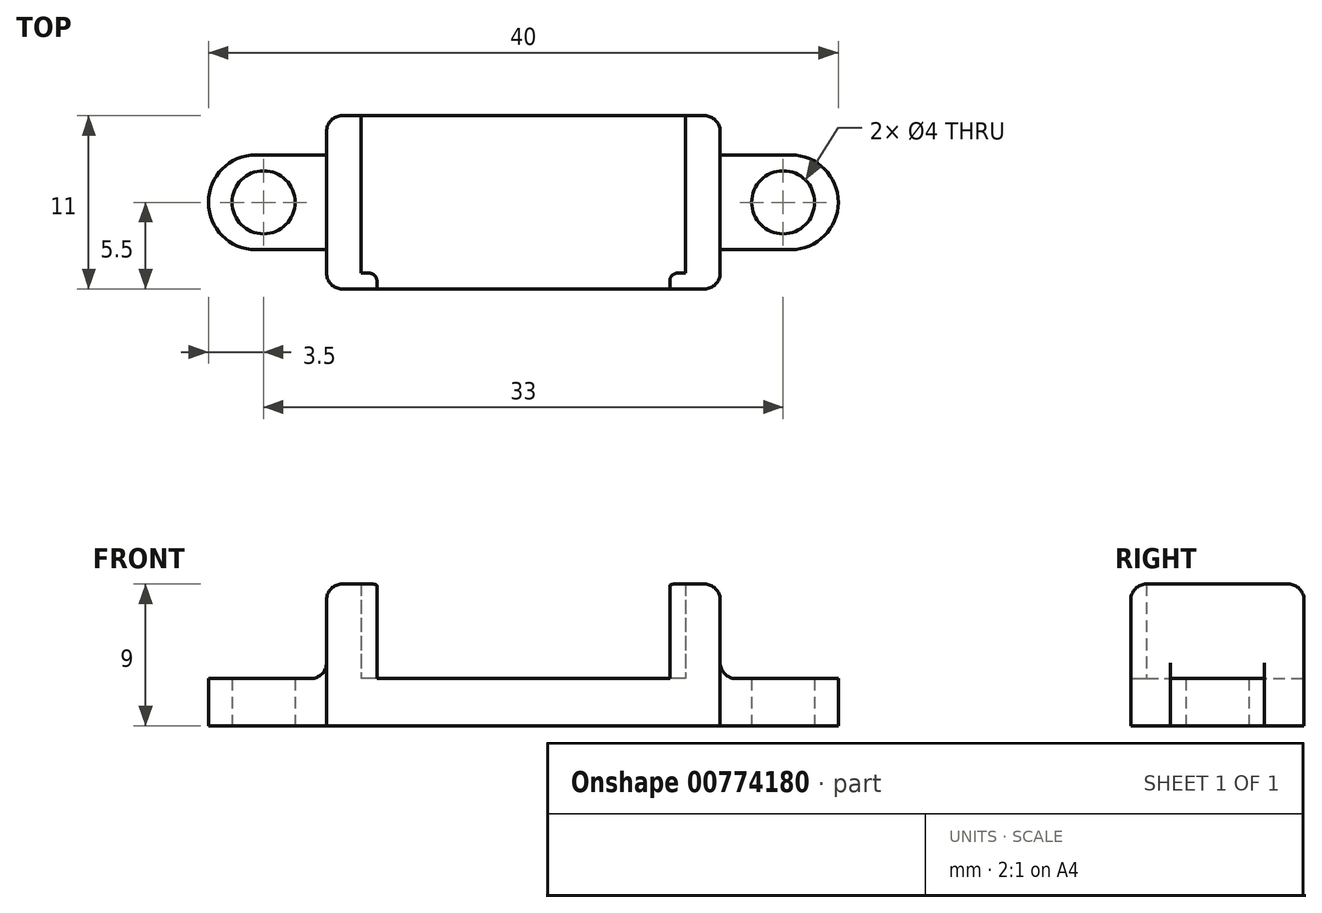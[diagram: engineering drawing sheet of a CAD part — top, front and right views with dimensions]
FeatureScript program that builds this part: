
annotation { "Feature Type Name" : "Feature", "Feature Type Description" : "" }
export const myFeature = defineFeature(function(context is Context, id is Id, definition is map)
    precondition{}
    {
        {
            var Q0;
            Q0=qCreatedBy(makeId("Top.planeOp"),FACE);
            var sketch = newSketch(context, id + "F0", { "sketchPlane" : qUnion([Q0])});
            skLineSegment(sketch, "E0.bottom", {"start": v(12.5, -5.5) * mm, "end": v(-12.5, -5.5) * mm});
            skLineSegment(sketch, "E0.top", {"start": v(12.5, 5.5) * mm, "end": v(-12.5, 5.5) * mm});
            skLineSegment(sketch, "E0.left", {"start": v(12.5, -5.5) * mm, "end": v(12.5, 5.5) * mm});
            skLineSegment(sketch, "E0.right", {"start": v(-12.5, -5.5) * mm, "end": v(-12.5, 5.5) * mm});
            skPoint(sketch, "E0.middle", {"position": v(0, 0) * mm});
            skSolve(sketch);
        }
        {
            var Q0;
            Q0 = qSketchRegion(id + "F0", true);
            extrude(context, id + "F1", {"entities" : qUnion([Q0]), "depth" : 9 * mm, "offsetDistance" : 25 * mm});
        }
        {
            var Q0;
            Q0=qCreatedBy(makeId("Top.planeOp"),FACE);
            var sketch = newSketch(context, id + "F2", { "sketchPlane" : qUnion([Q0])});
            skLineSegment(sketch, "E1.bottom", {"start": v(10.3, -5) * mm, "end": v(-10.3, -5) * mm});
            skLineSegment(sketch, "E1.top", {"start": v(10.3, 5) * mm, "end": v(-10.3, 5) * mm});
            skLineSegment(sketch, "E1.left", {"start": v(10.3, -5) * mm, "end": v(10.3, 5) * mm});
            skLineSegment(sketch, "E1.right", {"start": v(-10.3, -5) * mm, "end": v(-10.3, 5) * mm});
            skPoint(sketch, "E1.middle", {"position": v(0, 0) * mm});
            skSolve(sketch);
        }
        {
            var Q0;
            Q0 = qSketchRegion(id + "F2", true);
            extrude(context, id + "F3", {"entities" : qUnion([Q0]), "depth" : 6 * mm, "offsetDistance" : 25 * mm});
        }
        {
            var Q0;
            Q0=qCreatedBy(makeId("Top.planeOp"),FACE);
            var sketch = newSketch(context, id + "F4", { "sketchPlane" : qUnion([Q0])});
            skLineSegment(sketch, "E2.bottom", {"start": v(9.3, -5) * mm, "end": v(-9.3, -5) * mm});
            skLineSegment(sketch, "E2.top", {"start": v(9.3, 5) * mm, "end": v(-9.3, 5) * mm});
            skLineSegment(sketch, "E2.left", {"start": v(9.3, -5) * mm, "end": v(9.3, 5) * mm});
            skLineSegment(sketch, "E2.right", {"start": v(-9.3, -5) * mm, "end": v(-9.3, 5) * mm});
            skPoint(sketch, "E2.middle", {"position": v(0, 0) * mm});
            skSolve(sketch);
        }
        {
            var Q0;
            Q0 = qSketchRegion(id + "F4", true);
            extrude(context, id + "F5", {"entities" : qUnion([Q0]), "depth" : 6 * mm, "offsetDistance" : 25 * mm});
        }
        {
            var Q0;
            Q0=makeQuery(id+"F5.opExtrude","SWEPT_BODY",BODY,{"disambiguationData":[OSD([sQuery(id+"F4.wireOp",EDGE,"E2.bottom"),sQuery(id+"F4.wireOp",EDGE,"E2.top"),sQuery(id+"F4.wireOp",EDGE,"E2.left"),sQuery(id+"F4.wireOp",EDGE,"E2.right")])]});
            transform(context, id + "F6", {"entities" : qUnion([Q0]), "transformType" : TransformType.TRANSLATION_3D, "dx" : 0 * mm, "dy" : -5 * mm, "dz" : 0 * mm, "makeCopy" : false});
        }
        {
            var Q0;
            Q0=makeQuery(id+"F3.opExtrude","SWEPT_BODY",BODY,{"disambiguationData":[OSD([sQuery(id+"F2.wireOp",EDGE,"E1.bottom"),sQuery(id+"F2.wireOp",EDGE,"E1.top"),sQuery(id+"F2.wireOp",EDGE,"E1.left"),sQuery(id+"F2.wireOp",EDGE,"E1.right")])]});
            var Q1;
            Q1=makeQuery(id+"F5.opExtrude","SWEPT_BODY",BODY,{"disambiguationData":[OSD([sQuery(id+"F4.wireOp",EDGE,"E2.bottom"),sQuery(id+"F4.wireOp",EDGE,"E2.top"),sQuery(id+"F4.wireOp",EDGE,"E2.left"),sQuery(id+"F4.wireOp",EDGE,"E2.right")])]});
            booleanBodies(context, id + "F7", {"operationType" : BooleanOperationType.UNION, "tools" : qUnion([Q0, Q1])});
        }
        {
            var Q0;
            Q0=makeQuery(id+"F7.opBoolean","INTERSECT",EDGE,{"derivedFrom":[makeQuery(id+"F3.opExtrude","SWEPT_FACE",FACE,{"disambiguationData":[OSD([sQuery(id+"F2.wireOp",EDGE,"E1.bottom")])]}),makeQuery(id+"F5.opExtrude","SWEPT_FACE",FACE,{"disambiguationData":[OSD([sQuery(id+"F4.wireOp",EDGE,"E2.right")])]})]});
            var Q1;
            Q1=makeQuery(id+"F7.opBoolean","INTERSECT",EDGE,{"derivedFrom":[makeQuery(id+"F3.opExtrude","SWEPT_FACE",FACE,{"disambiguationData":[OSD([sQuery(id+"F2.wireOp",EDGE,"E1.bottom")])]}),makeQuery(id+"F5.opExtrude","SWEPT_FACE",FACE,{"disambiguationData":[OSD([sQuery(id+"F4.wireOp",EDGE,"E2.left")])]})]});
            fillet(context, id + "F8", {"entities" : qUnion([Q0, Q1]), "radius" : 0.5 * mm, "tangentPropagation" : true, "allowEdgeOverflow" : false});
        }
        {
            var Q0;
            Q0=makeQuery(id+"F3.opExtrude","SWEPT_BODY",BODY,{"disambiguationData":[OSD([sQuery(id+"F2.wireOp",EDGE,"E1.bottom"),sQuery(id+"F2.wireOp",EDGE,"E1.top"),sQuery(id+"F2.wireOp",EDGE,"E1.left"),sQuery(id+"F2.wireOp",EDGE,"E1.right")])]});
            transform(context, id + "F9", {"entities" : qUnion([Q0]), "transformType" : TransformType.TRANSLATION_3D, "dx" : 0 * mm, "dy" : .5 * mm, "dz" : 3 * mm, "makeCopy" : false});
        }
        {
            var Q0;
            Q0=makeQuery(id+"F3.opExtrude","SWEPT_BODY",BODY,{"disambiguationData":[OSD([sQuery(id+"F2.wireOp",EDGE,"E1.bottom"),sQuery(id+"F2.wireOp",EDGE,"E1.top"),sQuery(id+"F2.wireOp",EDGE,"E1.left"),sQuery(id+"F2.wireOp",EDGE,"E1.right")])]});
            var Q1;
            Q1=makeQuery(id+"F1.opExtrude","SWEPT_BODY",BODY,{"disambiguationData":[OSD([sQuery(id+"F0.wireOp",EDGE,"E0.bottom"),sQuery(id+"F0.wireOp",EDGE,"E0.top"),sQuery(id+"F0.wireOp",EDGE,"E0.left"),sQuery(id+"F0.wireOp",EDGE,"E0.right")])]});
            booleanBodies(context, id + "F10", {"operationType" : BooleanOperationType.SUBTRACTION, "tools" : qUnion([Q0]), "targets" : qUnion([Q1])});
        }
        {
            var Q0;
            Q0=qCreatedBy(makeId("Top.planeOp"),FACE);
            var sketch = newSketch(context, id + "F11", { "sketchPlane" : qUnion([Q0])});
            skLineSegment(sketch, "E3.bottom", {"start": v(20, -3) * mm, "end": v(-20, -3) * mm});
            skLineSegment(sketch, "E3.top", {"start": v(20, 3) * mm, "end": v(-20, 3) * mm});
            skLineSegment(sketch, "E3.left", {"start": v(20, -3) * mm, "end": v(20, 3) * mm});
            skLineSegment(sketch, "E3.right", {"start": v(-20, -3) * mm, "end": v(-20, 3) * mm});
            skPoint(sketch, "E3.middle", {"position": v(0, 0) * mm});
            skLineSegment(sketch, "E4", {"start": v(0, 0) * mm, "end": v(-16.5, 0) * mm});
            skLineSegment(sketch, "E5", {"start": v(0, 0) * mm, "end": v(16.5, 0) * mm});
            skCircle(sketch, "E6", {"center": v(-16.5, 0) * mm, "radius": 2 * mm});
            skCircle(sketch, "E7", {"center": v(16.5, 0) * mm, "radius": 2 * mm});
            skSolve(sketch);
        }
        {
            var Q0;
            Q0 = qSketchRegion(id + "F11", true);
            extrude(context, id + "F12", {"entities" : qUnion([Q0]), "operationType" : NewBodyOperationType.ADD, "depth" : 3 * mm, "offsetDistance" : 25 * mm});
        }
        {
            var Q0;
            Q0=makeQuery(id+"F1.opExtrude","SWEPT_EDGE",EDGE,{"disambiguationData":[OSD([sQuery(id+"F0.wireOp",EDGE,"E0.top"),sQuery(id+"F0.wireOp",EDGE,"E0.right")])]});
            var Q1;
            Q1=makeQuery(id+"F1.opExtrude","SWEPT_EDGE",EDGE,{"disambiguationData":[OSD([sQuery(id+"F0.wireOp",EDGE,"E0.bottom"),sQuery(id+"F0.wireOp",EDGE,"E0.right")])]});
            var Q2;
            Q2=makeQuery(id+"F1.opExtrude","SWEPT_EDGE",EDGE,{"disambiguationData":[OSD([sQuery(id+"F0.wireOp",EDGE,"E0.bottom"),sQuery(id+"F0.wireOp",EDGE,"E0.left")])]});
            var Q3;
            Q3=makeQuery(id+"F1.opExtrude","SWEPT_EDGE",EDGE,{"disambiguationData":[OSD([sQuery(id+"F0.wireOp",EDGE,"E0.top"),sQuery(id+"F0.wireOp",EDGE,"E0.left")])]});
            var Q4;
            Q4=makeQuery(id+"F12.boolean.opBoolean","INTERSECT",EDGE,{"derivedFrom":[makeQuery(id+"F1.opExtrude","SWEPT_FACE",FACE,{"disambiguationData":[OSD([sQuery(id+"F0.wireOp",EDGE,"E0.left")])]}),makeQuery(id+"F12.opExtrude","CAP_FACE",FACE,{"disambiguationData":[OSD([sQuery(id+"F11.wireOp",EDGE,"E3.bottom"),sQuery(id+"F11.wireOp",EDGE,"E3.top"),sQuery(id+"F11.wireOp",EDGE,"E3.left"),sQuery(id+"F11.wireOp",EDGE,"E3.right"),sQuery(id+"F11.wireOp",EDGE,"E6"),sQuery(id+"F11.wireOp",EDGE,"E7")])],"isStart":false})]});
            var Q5;
            Q5=makeQuery(id+"F12.boolean.opBoolean","INTERSECT",EDGE,{"derivedFrom":[makeQuery(id+"F1.opExtrude","SWEPT_FACE",FACE,{"disambiguationData":[OSD([sQuery(id+"F0.wireOp",EDGE,"E0.right")])]}),makeQuery(id+"F12.opExtrude","CAP_FACE",FACE,{"disambiguationData":[OSD([sQuery(id+"F11.wireOp",EDGE,"E3.bottom"),sQuery(id+"F11.wireOp",EDGE,"E3.top"),sQuery(id+"F11.wireOp",EDGE,"E3.left"),sQuery(id+"F11.wireOp",EDGE,"E3.right"),sQuery(id+"F11.wireOp",EDGE,"E6"),sQuery(id+"F11.wireOp",EDGE,"E7")])],"isStart":false})]});
            var Q6;
            Q6=makeQuery(id+"F1.opExtrude","CAP_EDGE",EDGE,{"disambiguationData":[OSD([sQuery(id+"F0.wireOp",EDGE,"E0.right")])],"isStart":false});
            var Q7;
            Q7=makeQuery(id+"F1.opExtrude","CAP_EDGE",EDGE,{"disambiguationData":[OSD([sQuery(id+"F0.wireOp",EDGE,"E0.left")])],"isStart":false});
            var Q8;
            {var subQ0=sQuery(id+"F0.wireOp",EDGE,"E0.right");var subQ1=sQuery(id+"F0.wireOp",EDGE,"E0.top");Q8=makeQuery(id+"F10.opBoolean","SPLIT",EDGE,{"disambiguationData":[TD([makeQuery(id+"F1.opExtrude","SWEPT_FACE",FACE,{"disambiguationData":[OSD([subQ0])]})])],"derivedFrom":makeQuery(id+"F1.opExtrude","CAP_EDGE",EDGE,{"disambiguationData":[OSD([subQ1])],"isStart":false})});}
            var Q9;
            {var subQ0=sQuery(id+"F0.wireOp",EDGE,"E0.left");var subQ1=sQuery(id+"F0.wireOp",EDGE,"E0.top");Q9=makeQuery(id+"F10.opBoolean","SPLIT",EDGE,{"disambiguationData":[TD([makeQuery(id+"F1.opExtrude","SWEPT_FACE",FACE,{"disambiguationData":[OSD([subQ0])]})])],"derivedFrom":makeQuery(id+"F1.opExtrude","CAP_EDGE",EDGE,{"disambiguationData":[OSD([subQ1])],"isStart":false})});}
            var Q10;
            {var subQ0=sQuery(id+"F0.wireOp",EDGE,"E0.bottom");var subQ1=sQuery(id+"F0.wireOp",EDGE,"E0.left");Q10=makeQuery(id+"F10.opBoolean","SPLIT",EDGE,{"disambiguationData":[TD([makeQuery(id+"F1.opExtrude","SWEPT_FACE",FACE,{"disambiguationData":[OSD([subQ1])]})])],"derivedFrom":makeQuery(id+"F1.opExtrude","CAP_EDGE",EDGE,{"disambiguationData":[OSD([subQ0])],"isStart":false})});}
            var Q11;
            {var subQ0=sQuery(id+"F0.wireOp",EDGE,"E0.bottom");var subQ1=sQuery(id+"F0.wireOp",EDGE,"E0.right");Q11=makeQuery(id+"F10.opBoolean","SPLIT",EDGE,{"disambiguationData":[TD([makeQuery(id+"F1.opExtrude","SWEPT_FACE",FACE,{"disambiguationData":[OSD([subQ1])]})])],"derivedFrom":makeQuery(id+"F1.opExtrude","CAP_EDGE",EDGE,{"disambiguationData":[OSD([subQ0])],"isStart":false})});}
            fillet(context, id + "F13", {"entities" : qUnion([Q0, Q1, Q2, Q3, Q4, Q5, Q6, Q7, Q8, Q9, Q10, Q11]), "radius" : 1 * mm, "tangentPropagation" : true, "allowEdgeOverflow" : false});
        }
        {
            var Q0;
            Q0=makeQuery(id+"F12.opExtrude","SWEPT_EDGE",EDGE,{"disambiguationData":[OSD([sQuery(id+"F11.wireOp",EDGE,"E3.bottom"),sQuery(id+"F11.wireOp",EDGE,"E3.right")])]});
            var Q1;
            Q1=makeQuery(id+"F12.opExtrude","SWEPT_EDGE",EDGE,{"disambiguationData":[OSD([sQuery(id+"F11.wireOp",EDGE,"E3.top"),sQuery(id+"F11.wireOp",EDGE,"E3.right")])]});
            var Q2;
            Q2=makeQuery(id+"F12.opExtrude","SWEPT_EDGE",EDGE,{"disambiguationData":[OSD([sQuery(id+"F11.wireOp",EDGE,"E3.top"),sQuery(id+"F11.wireOp",EDGE,"E3.left")])]});
            var Q3;
            Q3=makeQuery(id+"F12.opExtrude","SWEPT_EDGE",EDGE,{"disambiguationData":[OSD([sQuery(id+"F11.wireOp",EDGE,"E3.bottom"),sQuery(id+"F11.wireOp",EDGE,"E3.left")])]});
            fillet(context, id + "F14", {"entities" : qUnion([Q0, Q1, Q2, Q3]), "radius" : 3 * mm, "tangentPropagation" : true, "allowEdgeOverflow" : false});
        }
    });
